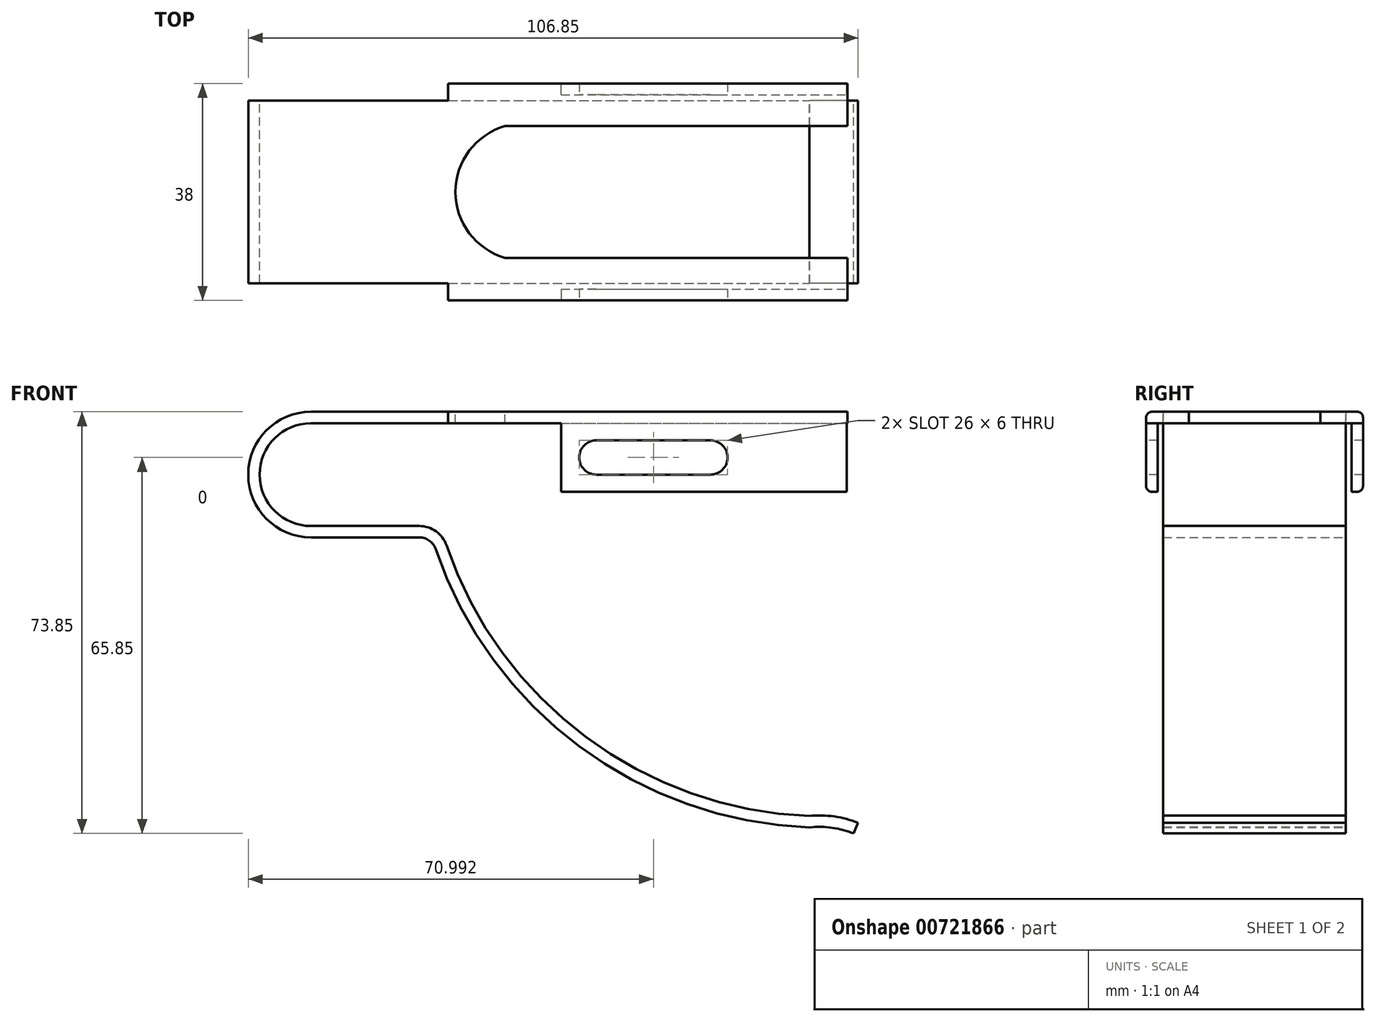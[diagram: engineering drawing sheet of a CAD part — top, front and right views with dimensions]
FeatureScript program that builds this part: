
annotation { "Feature Type Name" : "Feature", "Feature Type Description" : "" }
export const myFeature = defineFeature(function(context is Context, id is Id, definition is map)
    precondition{}
    {
        {
            var Q0;
            Q0=qCreatedBy(makeId("Front.planeOp"),FACE);
            var sketch = newSketch(context, id + "F0", { "sketchPlane" : qUnion([Q0])});
            skArc(sketch, "E0", {"start": v(0, 9) * mm, "mid": v(-9, 0) * mm, "end": v(0, -9) * mm});
            skLineSegment(sketch, "E1", {"start": v(0, 9) * mm, "end": v(94, 9) * mm});
            skLineSegment(sketch, "E2", {"start": v(0, -9) * mm, "end": v(19, -9) * mm});
            skArc(sketch, "E3", {"start": v(23.73, -12.39) * mm, "mid": v(48.17, -45.96) * mm, "end": v(87.32, -59.78) * mm});
            skArc(sketch, "E4", {"start": v(95.85, -61) * mm, "mid": v(91.66, -59.87) * mm, "end": v(87.32, -59.78) * mm});
            skPoint(sketch, "E5.visualSharp", {"position": v(22.67, -9) * mm});
            skArc(sketch, "E5.filletArc", {"start": v(23.73, -12.39) * mm, "mid": v(21.91, -9.93) * mm, "end": v(19, -9) * mm});
            skLineSegment(sketch, "E6.0", {"start": v(0, 11) * mm, "end": v(94, 11) * mm});
            skArc(sketch, "E6.1", {"start": v(0, 11) * mm, "mid": v(-11, 0) * mm, "end": v(0, -11) * mm});
            skArc(sketch, "E6.2", {"start": v(95.1, -62.85) * mm, "mid": v(91.31, -61.84) * mm, "end": v(87.39, -61.79) * mm});
            skArc(sketch, "E6.3", {"start": v(21.84, -13.03) * mm, "mid": v(47.03, -47.6) * mm, "end": v(87.39, -61.79) * mm});
            skArc(sketch, "E6.4", {"start": v(21.84, -13.03) * mm, "mid": v(20.75, -11.56) * mm, "end": v(19, -11) * mm});
            skLineSegment(sketch, "E6.5", {"start": v(0, -11) * mm, "end": v(19, -11) * mm});
            skLineSegment(sketch, "E7", {"start": v(94, 9) * mm, "end": v(94, 11) * mm});
            skLineSegment(sketch, "E8", {"start": v(95.1, -62.85) * mm, "end": v(95.85, -61) * mm});
            skSolve(sketch);
        }
        {
            var Q0;
            Q0 = qSketchRegion(id + "F0", true);
            extrude(context, id + "F1", {"entities" : qUnion([Q0]), "depth" : 16 * mm, "offsetDistance" : 25 * mm});
        }
        {
            var Q0;
            Q0=makeQuery(id+"F1.opExtrude","SWEPT_FACE",FACE,{"disambiguationData":[OSD([sQuery(id+"F0.wireOp",EDGE,"E6.0")])]});
            var sketch = newSketch(context, id + "F2", { "sketchPlane" : qUnion([Q0])});
            skLineSegment(sketch, "E9.bottom", {"start": v(24, -16) * mm, "end": v(94, -16) * mm});
            skLineSegment(sketch, "E9.top", {"start": v(24, -19) * mm, "end": v(94, -19) * mm});
            skLineSegment(sketch, "E9.left", {"start": v(24, -16) * mm, "end": v(24, -19) * mm});
            skLineSegment(sketch, "E9.right", {"start": v(94, -16) * mm, "end": v(94, -19) * mm});
            skSolve(sketch);
        }
        {
            var Q0;
            Q0 = qSketchRegion(id + "F2", true);
            extrude(context, id + "F3", {"entities" : qUnion([Q0]), "operationType" : NewBodyOperationType.ADD, "oppositeDirection" : true, "depth" : 2 * mm, "offsetDistance" : 25 * mm});
        }
        {
            var Q0;
            Q0=makeQuery(id+"F3.opExtrude","SWEPT_FACE",FACE,{"disambiguationData":[OSD([sQuery(id+"F2.wireOp",EDGE,"E9.top")])]});
            var sketch = newSketch(context, id + "F4", { "sketchPlane" : qUnion([Q0])});
            skLineSegment(sketch, "E10.bottom", {"start": v(43.85, 11) * mm, "end": v(93.85, 11) * mm});
            skLineSegment(sketch, "E10.top", {"start": v(43.85, -3) * mm, "end": v(93.85, -3) * mm});
            skLineSegment(sketch, "E10.left", {"start": v(43.85, 11) * mm, "end": v(43.85, -3) * mm});
            skLineSegment(sketch, "E10.right", {"start": v(93.85, 11) * mm, "end": v(93.85, -3) * mm});
            skSolve(sketch);
        }
        {
            var Q0;
            Q0 = qSketchRegion(id + "F4", true);
            extrude(context, id + "F5", {"entities" : qUnion([Q0]), "operationType" : NewBodyOperationType.ADD, "oppositeDirection" : true, "depth" : 2 * mm, "offsetDistance" : 25 * mm});
        }
        {
            var Q0;
            Q0=makeQuery(id+"F3.opExtrude","CAP_EDGE",EDGE,{"disambiguationData":[OSD([sQuery(id+"F2.wireOp",EDGE,"E9.top")])],"isStart":true});
            var Q1;
            Q1=makeQuery(id+"F5.opExtrude","CAP_EDGE",EDGE,{"disambiguationData":[OSD([sQuery(id+"F4.wireOp",EDGE,"E10.top")])],"isStart":true});
            fillet(context, id + "F6", {"entities" : qUnion([Q0, Q1]), "radius" : 1 * mm, "allowEdgeOverflow" : false});
        }
        {
            var Q0;
            Q0=makeQuery(id+"F1.opExtrude","SWEPT_BODY",BODY,{"disambiguationData":[OSD([sQuery(id+"F0.wireOp",EDGE,"E0"),sQuery(id+"F0.wireOp",EDGE,"E1"),sQuery(id+"F0.wireOp",EDGE,"E2"),sQuery(id+"F0.wireOp",EDGE,"E3"),sQuery(id+"F0.wireOp",EDGE,"E4"),sQuery(id+"F0.wireOp",EDGE,"E5.filletArc"),sQuery(id+"F0.wireOp",EDGE,"E6.0"),sQuery(id+"F0.wireOp",EDGE,"E6.1"),sQuery(id+"F0.wireOp",EDGE,"E6.2"),sQuery(id+"F0.wireOp",EDGE,"E6.3"),sQuery(id+"F0.wireOp",EDGE,"E6.4"),sQuery(id+"F0.wireOp",EDGE,"E6.5"),sQuery(id+"F0.wireOp",EDGE,"E7"),sQuery(id+"F0.wireOp",EDGE,"E8")])]});
            var Q1;
            Q1=qCreatedBy(makeId("Front.planeOp"),FACE);
            mirror(context, id + "F7", {"operationType" : NewBodyOperationType.ADD, "entities" : qUnion([Q0]), "mirrorPlane" : qUnion([Q1])});
        }
        {
            var Q0;
            {var subQ0=makeQuery(id+"F3.boolean.opBoolean","MERGE",FACE,{"derivedFrom":[makeQuery(id+"F1.opExtrude","SWEPT_FACE",FACE,{"disambiguationData":[OSD([sQuery(id+"F0.wireOp",EDGE,"E6.0")])]}),makeQuery(id+"F3.opExtrude","CAP_FACE",FACE,{"disambiguationData":[OSD([sQuery(id+"F2.wireOp",EDGE,"E9.bottom"),sQuery(id+"F2.wireOp",EDGE,"E9.top"),sQuery(id+"F2.wireOp",EDGE,"E9.left"),sQuery(id+"F2.wireOp",EDGE,"E9.right")])],"isStart":true})]});Q0=makeQuery(id+"F7.boolean.opBoolean","MERGE",FACE,{"derivedFrom":[subQ0,makeQuery(id+"F7.opPattern","COPY",FACE,{"derivedFrom":subQ0,"instanceName":"1"})]});}
            var sketch = newSketch(context, id + "F8", { "sketchPlane" : qUnion([Q0])});
            skArc(sketch, "E11", {"start": v(34, 11.53) * mm, "mid": v(25.32, 0) * mm, "end": v(34, -11.53) * mm});
            skLineSegment(sketch, "E12", {"start": v(34, 11.53) * mm, "end": v(94, 11.53) * mm});
            skLineSegment(sketch, "E13", {"start": v(34, -11.53) * mm, "end": v(94, -11.53) * mm});
            skSolve(sketch);
        }
        {
            var Q0;
            Q0=makeQuery(id+"F8.imprint","IMPRINT",FACE,{"disambiguationData":[TD([[makeQuery(id+"F8.imprint","IMPRINT",EDGE,{"derivedFrom":sQuery(id+"F8.wireOp",EDGE,"E11")}),1.0]])]});
            extrude(context, id + "F9", {"entities" : qUnion([Q0]), "operationType" : NewBodyOperationType.REMOVE, "oppositeDirection" : true, "depth" : 2 * mm, "offsetDistance" : 25 * mm});
        }
        {
            var Q0;
            Q0=makeQuery(id+"F5.boolean.opBoolean","MERGE",FACE,{"derivedFrom":[makeQuery(id+"F3.opExtrude","SWEPT_FACE",FACE,{"disambiguationData":[OSD([sQuery(id+"F2.wireOp",EDGE,"E9.top")])]}),makeQuery(id+"F5.opExtrude","CAP_FACE",FACE,{"disambiguationData":[OSD([sQuery(id+"F4.wireOp",EDGE,"E10.bottom"),sQuery(id+"F4.wireOp",EDGE,"E10.top"),sQuery(id+"F4.wireOp",EDGE,"E10.left"),sQuery(id+"F4.wireOp",EDGE,"E10.right")])],"isStart":true})]});
            var sketch = newSketch(context, id + "F10", { "sketchPlane" : qUnion([Q0])});
            skLineSegment(sketch, "E14", {"start": v(50, 3) * mm, "end": v(70, 3) * mm});
            skArc(sketch, "E15.0.startCap", {"start": v(50, 0) * mm, "mid": v(47, 3) * mm, "end": v(50, 6) * mm});
            skArc(sketch, "E15.0.endCap", {"start": v(70, 6) * mm, "mid": v(73, 3) * mm, "end": v(70, 0) * mm});
            skLineSegment(sketch, "E15.0.left", {"start": v(50, 6) * mm, "end": v(70, 6) * mm});
            skLineSegment(sketch, "E15.0.right", {"start": v(50, 0) * mm, "end": v(70, 0) * mm});
            skSolve(sketch);
        }
        {
            var Q0;
            Q0 = qSketchRegion(id + "F10", true);
            extrude(context, id + "F11", {"entities" : qUnion([Q0]), "operationType" : NewBodyOperationType.REMOVE, "endBound" : BoundingType.THROUGH_ALL, "oppositeDirection" : true, "depth" : 25 * mm, "offsetDistance" : 25 * mm});
        }
    });
